# Revit family: Vents_TT_2016_19.08
name_source: partatom
category: Оборудование
revit_build: Autodesk Revit 2016 (Build: 20160314_0715(x64)
units: mm (PartAtom-declared; Revit-internal decimal feet)

## family parameters
Всегда вертикально = Нет
На основе рабочей плоскости = Нет
Общий = Нет
При загрузке вырезать с полостями = Нет
Размер круглого соединителя = Использовать диаметр
Тип детали = Вставляется
Точка расчета площади = Нет

## types (5) — shared parameters
CAT0 = Да
CAT1 = Да
CAT2 = Да
Certification = by Manifacturer
Current.Max = 0 А
Current.Min = 0 А
EC motor = Нет
HH1 = 50 мм
Ingress Protection Rating = IPX4
L8 = 82 мм
LL4 = 41 мм
Motor IP Rating = IPX4
R3 = 49 мм
RR4 = 12 мм
URL = https://ventilation-system.com
Variable Speed Drive = Нет
Voltage = 230 В
W = 500 мм
WW1 = 50 мм
WW2 = 52 мм
Группа модели = ТТ
Изготовитель = VENTS
Описание = Inline mixed-flow fan
Угол = 60.00°

## per-type parameters (varying)
| type | D | FlowMax | FlowMin | HH2 | HH3 | LL1 | LL2 | LL3 | LL6 | LL7 | MC Product Code | Mass | PC | PE | Power max | Power min | R1 | R2 | RR3 | Service Zone | Service Zone 1 | Service Zone 2 | Sound Pressure Level at 3m  dBA (Min/Max) |
| TT 150 | 150 мм | 520.0 м³/ч | 405.0 м³/ч | 49 мм | 112 мм | 148 мм | 115 мм | 55 мм | 43 мм | 98 мм | ТТ 150 | 3.19 кг | 118 мм | 133 мм | 60 Вт | 29 Вт | 73 мм | 112 мм | 49 мм | 162 мм | 243 мм | 295 мм | 33/44 |
| TT 125S | 125 мм | 320.0 м³/ч | 240.0 м³/ч | 49 мм | 112 мм | 148 мм | 115 мм | 55 мм | 43 мм | 98 мм | ТТ 125 S | 3.14 кг | 118 мм | 133 мм | 54 Вт | 28 Вт | 62 мм | 112 мм | 49 мм | 162 мм | 243 мм | 295 мм | 31/42 |
| TT 160 | 160 мм | 520.0 м³/ч | 405.0 м³/ч | 49 мм | 117 мм | 148 мм | 115 мм | 55 мм | 43 мм | 98 мм | ТТ 160 | 3.22 кг | 118 мм | 133 мм | 60 Вт | 29 Вт | 79 мм | 117 мм | 49 мм | 167 мм | 253 мм | 295 мм | 33/44 |
| TT 125 | 125 мм | 280.0 м³/ч | 220.0 м³/ч | 58 мм | 84 мм | 123 мм | 95 мм | 59 мм | 65 мм | 124 мм | ТТ 125 | 1.79 кг | 100 мм | 90 мм | 37 Вт | 23 Вт | 62 мм | 84 мм | 21 мм | 134 мм | 187 мм | 246 мм | 28/37 |
| TT 100 | 100 мм | 187.0 м³/ч | 145.0 м³/ч | 49 мм | 84 мм | 123 мм | 98 мм | 55 мм | 43 мм | 98 мм | ТТ 100 | 1.45 кг | 100 мм | 91 мм | 33 Вт | 21 Вт | 48 мм | 84 мм | 21 мм | 134 мм | 187 мм | 246 мм | 27/36 |

## geometry (parser evidence)
native form markers: Blend x4, Sweep x2
no freeform markers — native parametric forms only
